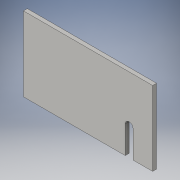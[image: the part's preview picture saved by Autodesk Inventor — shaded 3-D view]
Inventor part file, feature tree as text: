
AUTODESK INVENTOR PART (.ipt)
format: ipt  version: 2016 (Build 200138000, 138)  size: 98,816 bytes
history: native  units: in
note: dims shown in document units (in); Inventor stores cm internally (conversion verified against a paired STEP export)
features: extrude x1, sketch x1
ambient origin geometry x8: Origin, YZ Plane, XZ Plane, XY Plane, X Axis, Y Axis, Z Axis, Center Point
bodies: Solid1 (feature_tree)
feature tree (2):
  extrude  "Extrusion1"  Depth=9.5in
  sketch  "Sketch1"  dims[d0=16.5in d1=9.5in d2=3.0in d3=3.5in d4=1.0in d5=3.5in d6=0.5in d7=0.0in]
